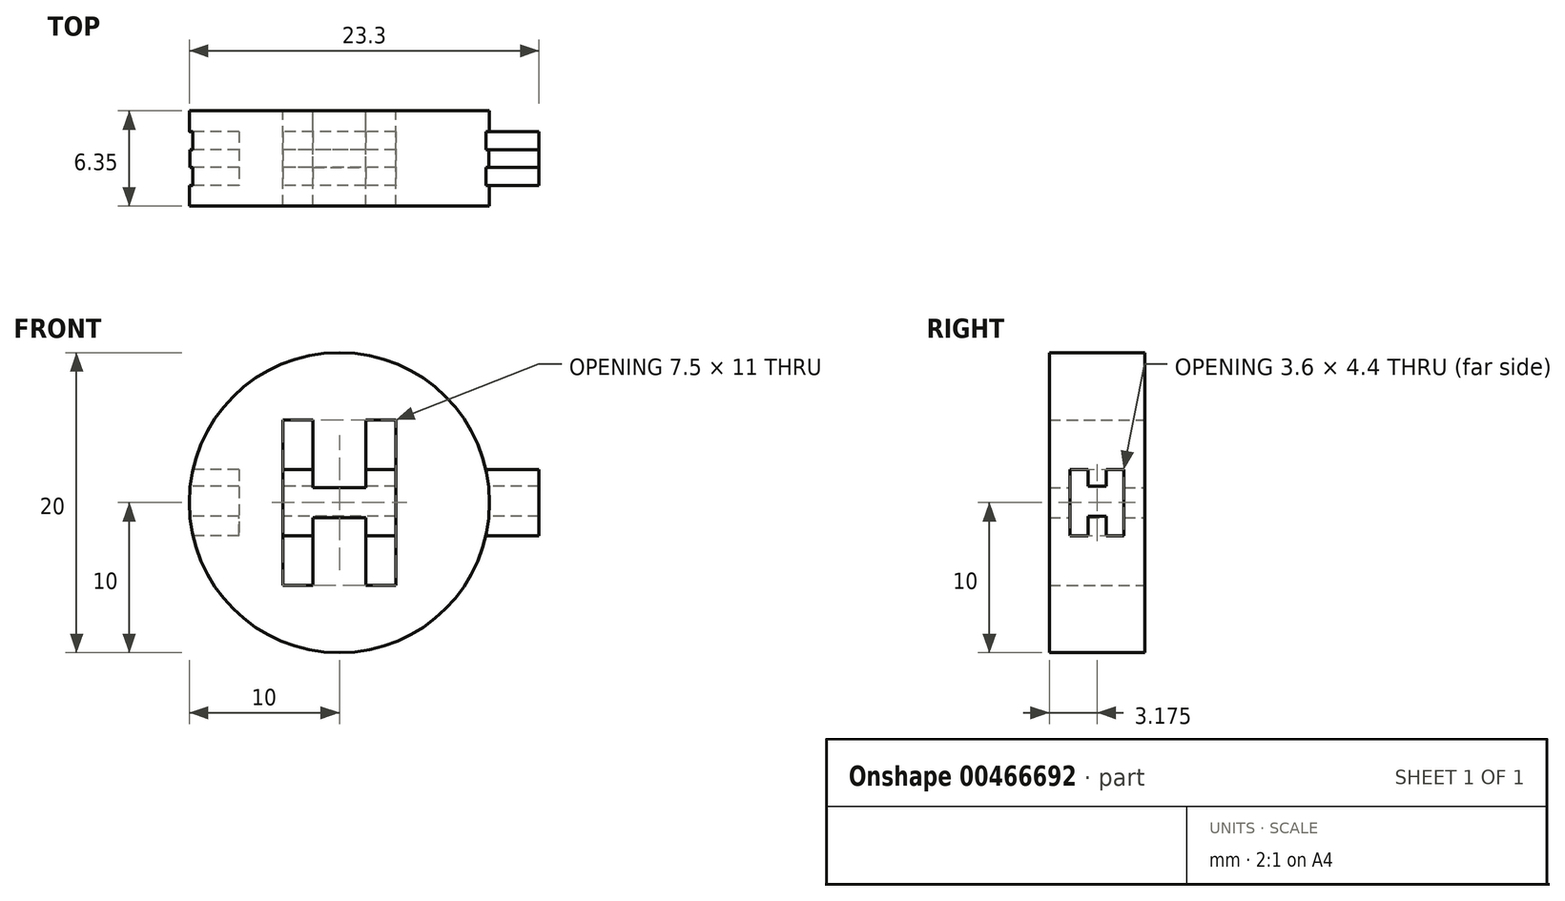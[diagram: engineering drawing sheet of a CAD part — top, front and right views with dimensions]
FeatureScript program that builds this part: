
annotation { "Feature Type Name" : "Feature", "Feature Type Description" : "" }
export const myFeature = defineFeature(function(context is Context, id is Id, definition is map)
    precondition{}
    {
        {
            var Q0;
            Q0=qCreatedBy(makeId("Front.planeOp"),FACE);
            var sketch = newSketch(context, id + "F0", { "sketchPlane" : qUnion([Q0])});
            skCircle(sketch, "E0", {"center": v(0, 0) * mm, "radius": 10 * mm});
            skLineSegment(sketch, "E1.bottom", {"start": v(-3.75, -1) * mm, "end": v(3.75, -1) * mm});
            skLineSegment(sketch, "E1.top", {"start": v(-3.75, 1) * mm, "end": v(3.75, 1) * mm});
            skLineSegment(sketch, "E1.left", {"start": v(-3.75, -1) * mm, "end": v(-3.75, 1) * mm});
            skLineSegment(sketch, "E1.right", {"start": v(3.75, -1) * mm, "end": v(3.75, 1) * mm});
            skLineSegment(sketch, "E2.bottom", {"start": v(-3.75, -1) * mm, "end": v(-1.75, -1) * mm});
            skLineSegment(sketch, "E2.top", {"start": v(-3.75, -5.5) * mm, "end": v(-1.75, -5.5) * mm});
            skLineSegment(sketch, "E2.left", {"start": v(-3.75, -1) * mm, "end": v(-3.75, -5.5) * mm});
            skLineSegment(sketch, "E2.right", {"start": v(-1.75, -1) * mm, "end": v(-1.75, -5.5) * mm});
            skLineSegment(sketch, "E3.bottom", {"start": v(3.75, -1) * mm, "end": v(1.75, -1) * mm});
            skLineSegment(sketch, "E3.top", {"start": v(3.75, -5.5) * mm, "end": v(1.75, -5.5) * mm});
            skLineSegment(sketch, "E3.left", {"start": v(3.75, -1) * mm, "end": v(3.75, -5.5) * mm});
            skLineSegment(sketch, "E3.right", {"start": v(1.75, -1) * mm, "end": v(1.75, -5.5) * mm});
            skLineSegment(sketch, "E4.bottom", {"start": v(-3.75, 1) * mm, "end": v(-1.75, 1) * mm});
            skLineSegment(sketch, "E4.top", {"start": v(-3.75, 5.5) * mm, "end": v(-1.75, 5.5) * mm});
            skLineSegment(sketch, "E4.left", {"start": v(-3.75, 1) * mm, "end": v(-3.75, 5.5) * mm});
            skLineSegment(sketch, "E4.right", {"start": v(-1.75, 1) * mm, "end": v(-1.75, 5.5) * mm});
            skLineSegment(sketch, "E5.bottom", {"start": v(3.75, 1) * mm, "end": v(1.75, 1) * mm});
            skLineSegment(sketch, "E5.top", {"start": v(3.75, 5.5) * mm, "end": v(1.75, 5.5) * mm});
            skLineSegment(sketch, "E5.left", {"start": v(3.75, 1) * mm, "end": v(3.75, 5.5) * mm});
            skLineSegment(sketch, "E5.right", {"start": v(1.75, 1) * mm, "end": v(1.75, 5.5) * mm});
            skSolve(sketch);
        }
        {
            var Q0;
            Q0 = qSketchRegion(id + "F0", true);
            var Q1;
            Q1 = qSketchRegion(id + "FnNhmq3yAJwvCMO_1", true);
            extrude(context, id + "F1", {"entities" : qUnion([Q0, Q1]), "depth" : 6.35 * mm});
        }
        {
            var Q0;
            Q0=qCreatedBy(makeId("Right.planeOp"),FACE);
            cPlane(context, id + "F2", {"entities" : qUnion([Q0]), "cplaneType" : CPlaneType.OFFSET, "offset" : 9.7 * mm, "oppositeDirection" : true, "width" : 150 * mm, "height" : 150 * mm});
        }
        {
            var Q0;
            Q0=qCreatedBy(id+"F2.planeOp",FACE);
            var sketch = newSketch(context, id + "F3", { "sketchPlane" : qUnion([Q0])});
            skLineSegment(sketch, "E6", {"start": v(-1.38, 0) * mm, "end": v(-1.38, 2.2) * mm});
            skLineSegment(sketch, "E7", {"start": v(-1.38, 2.2) * mm, "end": v(-1.38, 0) * mm});
            skLineSegment(sketch, "E8", {"start": v(-1.38, 0) * mm, "end": v(-1.38, -2.2) * mm});
            skLineSegment(sketch, "E9", {"start": v(-1.38, 2.2) * mm, "end": v(-2.58, 2.2) * mm});
            skLineSegment(sketch, "E10", {"start": v(-2.58, 2.2) * mm, "end": v(-2.58, 1.1) * mm});
            skLineSegment(sketch, "E11", {"start": v(-2.58, 1.1) * mm, "end": v(-3.78, 1.1) * mm});
            skLineSegment(sketch, "E12", {"start": v(-3.78, 1.1) * mm, "end": v(-3.78, 2.2) * mm});
            skLineSegment(sketch, "E13", {"start": v(-3.78, 2.2) * mm, "end": v(-4.98, 2.2) * mm});
            skLineSegment(sketch, "E14", {"start": v(-4.98, 2.2) * mm, "end": v(-4.98, -2.2) * mm});
            skLineSegment(sketch, "E15", {"start": v(-4.97, -2.2) * mm, "end": v(-3.77, -2.2) * mm});
            skLineSegment(sketch, "E16", {"start": v(-3.77, -2.2) * mm, "end": v(-3.77, -0.9) * mm});
            skLineSegment(sketch, "E17", {"start": v(-3.78, -0.9) * mm, "end": v(-2.58, -0.9) * mm});
            skLineSegment(sketch, "E18", {"start": v(-2.58, -0.9) * mm, "end": v(-2.58, -2.2) * mm});
            skLineSegment(sketch, "E19", {"start": v(-2.58, -2.2) * mm, "end": v(-1.38, -2.2) * mm});
            skSolve(sketch);
        }
        {
            var Q0;
            Q0 = qSketchRegion(id + "F3", true);
            extrude(context, id + "F4", {"entities" : qUnion([Q0]), "operationType" : NewBodyOperationType.ADD, "depth" : 23 * mm});
        }
        {
            var Q0;
            Q0 = qSketchRegion(id + "F3", true);
            extrude(context, id + "F5", {"entities" : qUnion([Q0]), "operationType" : NewBodyOperationType.REMOVE, "depth" : 3 * mm});
        }
        {
            var Q0;
            Q0 = qSketchRegion(id + "F3", true);
            extrude(context, id + "F6", {"entities" : qUnion([Q0]), "operationType" : NewBodyOperationType.REMOVE, "oppositeDirection" : true, "depth" : 25 * mm});
        }
    });
